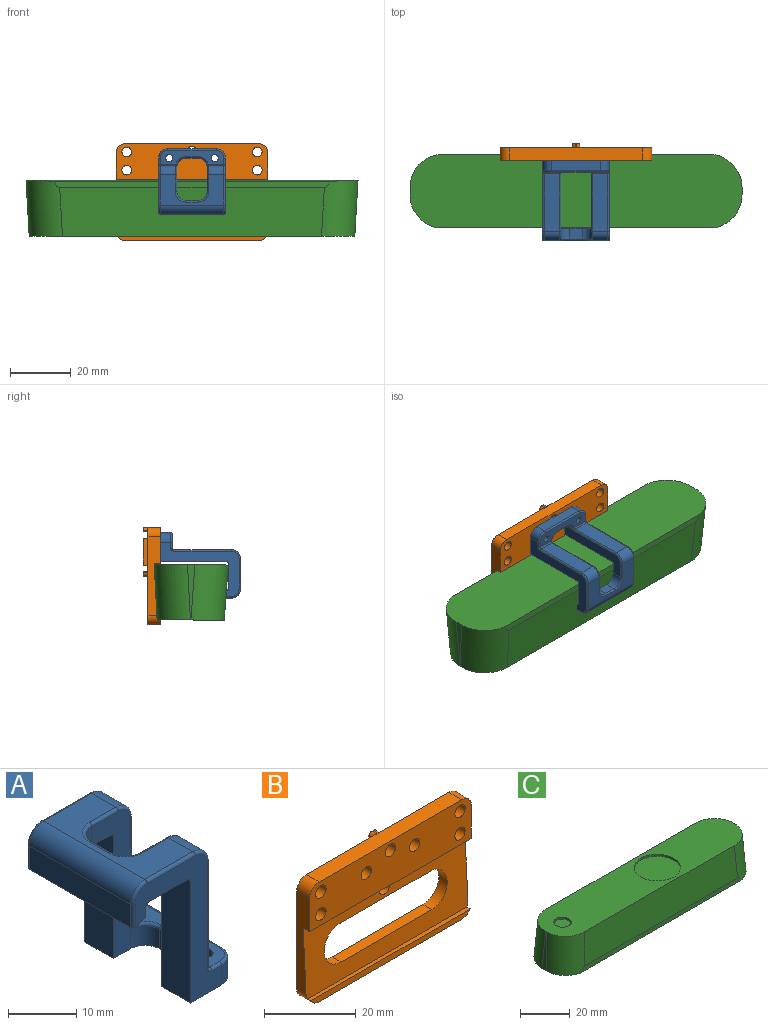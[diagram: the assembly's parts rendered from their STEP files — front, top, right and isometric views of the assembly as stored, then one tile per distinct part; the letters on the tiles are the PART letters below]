
ASSEMBLY  parts=3 mates=2
PART A: 65 faces, bbox 22x22.5x26.7 mm
  f0: cylinder r=3mm len=4.5mm, axis (0,0,1), area 16.7mm2, adj f3,f17,f20,f42,f45
  f1: plane 22x8.4mm, normal (0,0,-1), area 118.7mm2, adj f13,f14,f17,f18,f19,f24,f25,f62
  f2: plane 22x6mm, normal (-1,0,0), area 132mm2, adj f3,f13,f17,f64
  f3: plane 22x9.5mm, normal (0,0,-1), area 135mm2, adj f0,f2,f10,f11,f13,f14,f15,f16
  f4: plane 21x4.5mm, normal (0,0,1), area 60.4mm2, adj f15,f16,f38,f44,f45,f47,f48,f49
  f5: plane 19x5mm, normal (1,0,0), area 95mm2, adj f23,f37,f38,f39
  f6: plane 21x10mm, normal (0,0,1), area 116.3mm2, adj f22,f23,f26,f31,f32,f34,f36,f40
  f7: plane 21x4.19mm, normal (-1,0,0), area 88mm2, adj f8,f26,f29,f61
  f8: plane 22x2.6mm, normal (0.26,0,-0.97), area 59.1mm2, adj f7,f9,f13,f14,f29,f61
  f9: plane 22x2mm, normal (1,0,0), area 44mm2, adj f8,f13,f14,f63
  f10: plane 22x6mm, normal (-1,0,0), area 132mm2, adj f3,f14,f18,f62
  f11: plane 16x3.5mm, normal (1,0,0), area 56mm2, adj f3,f27,f28,f49
  f12: plane 19x5mm, normal (1,0,0), area 95mm2, adj f22,f51,f55,f57
  f13: plane 26x18mm, normal (0,-1,0), area 145.2mm2, adj f1,f2,f3,f8,f9,f28,f29,f30
  f14: plane 26x18mm, normal (0,1,0), area 145.2mm2, adj f1,f3,f8,f9,f10,f27,f54,f56
  f15: cylinder r=1.2mm len=4mm, axis (0,0,1), area 30.2mm2, adj f3,f4
  f16: cylinder r=1.2mm len=4mm, axis (0,0,1), area 30.2mm2, adj f3,f4
  f17: plane 26x8mm, normal (0,1,0), area 105.5mm2, adj f0,f1,f2,f3,f25,f31,f33,f39
  f18: plane 26x8mm, normal (0,-1,0), area 105.5mm2, adj f1,f3,f10,f21,f24,f43,f46,f51
  f19: plane 4x3.5mm, normal (1,0,0), area 14mm2, adj f1,f24,f25,f36
  f20: plane 4x3.5mm, normal (-1,0,0), area 14mm2, adj f0,f3,f21,f48
  f21: cylinder r=3mm len=4.5mm, axis (0,0,-1), area 16.7mm2, adj f3,f18,f20,f50,f53
  f22: cylinder r=3mm len=5mm, axis (0,1,0), area 23.6mm2, adj f6,f12,f46,f58
  f23: cylinder r=3mm len=5mm, axis (0,1,0), area 23.6mm2, adj f5,f6,f33,f35
  f24: cylinder r=3mm len=3.5mm, axis (0,0,1), area 16.5mm2, adj f1,f18,f19,f40
  f25: cylinder r=3mm len=3.5mm, axis (0,0,-1), area 16.5mm2, adj f1,f17,f19,f34
  f26: cylinder r=3mm len=21mm, axis (0,1,0), area 99mm2, adj f6,f7,f30,f60
  f27: cylinder r=3mm len=3.5mm, axis (0,0,1), area 16.5mm2, adj f3,f11,f14,f52
  f28: cylinder r=3mm len=3.5mm, axis (0,0,-1), area 16.5mm2, adj f3,f11,f13,f47
  f29: cylinder r=0.5mm len=4.19mm, axis (0,0,1), area 3.3mm2, adj f7,f8,f13,f30
  f30: torus R=2.5mm, axis (0,-1,0), area 3.5mm2, adj f13,f26,f29,f32
  f31: cylinder r=0.5mm len=5.5mm, axis (-1,0,0), area 4.3mm2, adj f6,f17,f33,f34
  f32: cylinder r=0.5mm len=10mm, axis (1,0,0), area 7.9mm2, adj f6,f13,f30,f35
  f33: torus R=2.5mm, axis (0,1,0), area 3.5mm2, adj f17,f23,f31,f39
  f34: torus R=3.5mm, axis (0,0,1), area 3.9mm2, adj f6,f25,f31,f36
  f35: torus R=2.5mm, axis (0,-1,0), area 3.5mm2, adj f13,f23,f32,f37
  f36: cylinder r=0.5mm len=4mm, axis (0,1,0), area 3.1mm2, adj f6,f19,f34,f40
  f37: cylinder r=0.5mm len=19mm, axis (0,0,-1), area 14.9mm2, adj f5,f13,f35,f41
  f38: cylinder r=0.5mm len=5.15mm, axis (0,-1,0), area 4mm2, adj f4,f5,f41,f42
  f39: cylinder r=0.5mm len=19mm, axis (0,0,1), area 14.9mm2, adj f5,f17,f33,f42
  f40: torus R=3.5mm, axis (0,0,1), area 3.9mm2, adj f6,f24,f36,f43
  f41: torus R=1mm, axis (0,-1,0), area 0.8mm2, adj f13,f37,f38,f44
  f42: bspline ~1.22x1.07mm, area 0.8mm2, adj f0,f38,f39,f45
  f43: cylinder r=0.5mm len=5.5mm, axis (1,0,0), area 4.3mm2, adj f6,f18,f40,f46
  f44: cylinder r=0.5mm len=2mm, axis (1,0,0), area 1.6mm2, adj f4,f13,f41,f47
  f45: torus R=3.5mm, axis (0,0,1), area 3.2mm2, adj f0,f4,f42,f48
  f46: torus R=2.5mm, axis (0,1,0), area 3.5mm2, adj f18,f22,f43,f51
  f47: torus R=2.5mm, axis (0,0,1), area 3.5mm2, adj f4,f28,f44,f49
  f48: cylinder r=0.5mm len=4mm, axis (0,-1,0), area 3.1mm2, adj f4,f20,f45,f50
  f49: cylinder r=0.5mm len=16mm, axis (0,1,0), area 12.6mm2, adj f4,f11,f47,f52
  f50: torus R=3.5mm, axis (0,0,1), area 3.2mm2, adj f4,f21,f48,f53
  f51: cylinder r=0.5mm len=19mm, axis (0,0,-1), area 14.9mm2, adj f12,f18,f46,f53
  f52: torus R=2.5mm, axis (0,0,1), area 3.5mm2, adj f4,f27,f49,f54
  f53: bspline ~1.14x1.11mm, area 0.8mm2, adj f21,f50,f51,f55
  f54: cylinder r=0.5mm len=2mm, axis (-1,0,0), area 1.6mm2, adj f4,f14,f52,f56
  f55: cylinder r=0.5mm len=5.15mm, axis (0,-1,0), area 4mm2, adj f4,f12,f53,f56
  f56: torus R=1mm, axis (0,-1,0), area 0.8mm2, adj f14,f54,f55,f57
  f57: cylinder r=0.5mm len=19mm, axis (0,0,1), area 14.9mm2, adj f12,f14,f56,f58
  f58: torus R=2.5mm, axis (0,-1,0), area 3.5mm2, adj f14,f22,f57,f59
  f59: cylinder r=0.5mm len=10mm, axis (-1,0,0), area 7.9mm2, adj f6,f14,f58,f60
  f60: torus R=2.5mm, axis (0,-1,0), area 3.5mm2, adj f14,f26,f59,f61
  f61: cylinder r=0.5mm len=4.19mm, axis (0,0,-1), area 3.3mm2, adj f7,f8,f14,f60
  f62: cylinder r=0.5mm len=6mm, axis (0,1,0), area 4.7mm2, adj f1,f10,f14,f18
  f63: cylinder r=0.5mm len=22mm, axis (0,-1,0), area 17.3mm2, adj f1,f9,f13,f14
  f64: cylinder r=0.5mm len=6mm, axis (0,1,0), area 4.7mm2, adj f1,f2,f13,f17
PART B: 39 faces, bbox 50x5.5x32 mm
  f0: plane 8.88x1.5mm, normal (1,0,0), area 13.3mm2, adj f4,f6,f33,f34
  f1: plane 1.5x0.44mm, normal (1,0,0), area 0.7mm2, adj f5,f6,f33,f35
  f2: plane 8.88x1.5mm, normal (-1,0,0), area 13.3mm2, adj f4,f6,f33,f34
  f3: plane 1.5x0.44mm, normal (-1,0,0), area 0.7mm2, adj f5,f6,f33,f36
  f4: plane 8.88x2.4mm, normal (0,1,0), area 19.5mm2, adj f0,f2,f33,f34
  f5: plane 2.4x1.44mm, normal (0,1,0), area 2.1mm2, adj f1,f3,f26,f33,f35,f36
  f6: plane 50x32mm, normal (0,1,0), area 1145.6mm2, adj f0,f1,f2,f3,f9,f10,f11,f12
  f7: plane 50x18.7mm, normal (0,-1,0.05), area 568.8mm2, adj f9,f10,f14,f15,f22,f23,f26,f27
  f8: plane 50x11.8mm, normal (0,-1,0), area 529.8mm2, adj f9,f10,f12,f15,f16,f17,f18,f19
  f9: plane 26x4mm, normal (1,0,0), area 77.7mm2, adj f6,f7,f8,f15,f23,f24
  f10: plane 26x4mm, normal (-1,0,0), area 77.7mm2, adj f6,f7,f8,f15,f22,f25
  f11: plane 44x4mm, normal (0,0,-1), area 176mm2, adj f6,f13,f22,f23
  f12: plane 44x5.5mm, normal (0,0,1), area 176.6mm2, adj f6,f8,f24,f25,f32,f37,f38
  f13: plane 49.2x1.5mm, normal (0,-1,0), area 71.5mm2, adj f11,f14,f22,f23
  f14: plane 49.2x1mm, normal (0,0,1), area 49.2mm2, adj f7,f13,f22,f23
  f15: plane 50x1.98mm, normal (0,0,-1), area 99mm2, adj f7,f8,f9,f10
  f16: cylinder r=1.6mm len=4mm, axis (0,-1,0), area 40.2mm2, adj f6,f8
  f17: cylinder r=1.6mm len=4mm, axis (0,-1,0), area 40.2mm2, adj f6,f8
  f18: cylinder r=1.6mm len=4mm, axis (0,-1,0), area 40.2mm2, adj f6,f8
  f19: cylinder r=1.6mm len=4mm, axis (0,-1,0), area 40.2mm2, adj f6,f8
  f20: cylinder r=1.6mm len=4mm, axis (0,-1,0), area 40.2mm2, adj f6,f8
  f21: cylinder r=1.6mm len=4mm, axis (0,-1,0), area 40.2mm2, adj f6,f8
  f22: cylinder r=3mm len=4mm, axis (0,-1,0), area 17.2mm2, adj f6,f7,f10,f11,f13,f14
  f23: cylinder r=3mm len=4mm, axis (0,1,0), area 17.2mm2, adj f6,f7,f9,f11,f13,f14
  f24: cylinder r=3mm len=4mm, axis (0,-1,0), area 18.8mm2, adj f6,f8,f9,f12
  f25: cylinder r=3mm len=4mm, axis (0,1,0), area 18.8mm2, adj f6,f8,f10,f12
  f26: plane 28x3.74mm, normal (0,0,-1), area 63.3mm2, adj f5,f6,f7,f28,f29,f35,f36
  f27: plane 28x2.76mm, normal (0,0,1), area 77.4mm2, adj f6,f7,f28,f29
  f28: cylinder r=5mm len=10mm, axis (0,1,0), area 39.3mm2, adj f6,f7,f26,f27
  f29: cylinder r=5mm len=10mm, axis (0,-1,0), area 39.3mm2, adj f6,f7,f26,f27
  f30: plane 1.5x0.44mm, normal (1,0,0), area 0.7mm2, adj f6,f32,f34,f38
  f31: plane 1.5x0.44mm, normal (-1,0,0), area 0.7mm2, adj f6,f32,f34,f37
  f32: plane 2.4x1.44mm, normal (0,1,0), area 2.1mm2, adj f12,f30,f31,f34,f37,f38
  f33: cylinder r=1.6mm len=3.69mm, axis (0,1,0), area 29.3mm2, adj f0,f1,f2,f3,f4,f5,f6,f7
  f34: cylinder r=1.6mm len=5.5mm, axis (0,1,0), area 48.4mm2, adj f0,f2,f4,f6,f8,f30,f31,f32
  f35: cylinder r=1mm len=1.5mm, axis (0,-1,0), area 2.4mm2, adj f1,f5,f6,f26
  f36: cylinder r=1mm len=1.5mm, axis (0,1,0), area 2.4mm2, adj f3,f5,f6,f26
  f37: cylinder r=1mm len=1.5mm, axis (0,1,0), area 2.4mm2, adj f6,f12,f31,f32
  f38: cylinder r=1mm len=1.5mm, axis (0,-1,0), area 2.4mm2, adj f6,f12,f30,f32
PART C: 16 faces, bbox 109.4x24.4x18.8 mm
  f0: plane 18.23x2.44mm, normal (-1,0,0.06), area 23.8mm2, adj f1,f3,f8,f9
  f1: plane 109.4x24.13mm, normal (0,0,-1), area 2541.9mm2, adj f0,f2,f4,f5,f8,f9,f10,f11
  f2: plane 18.23x2.44mm, normal (1,0,0.06), area 23.8mm2, adj f1,f3,f10,f11
  f3: plane 107.31x22.13mm, normal (0,0,1), area 1960.5mm2, adj f0,f2,f6,f7,f8,f9,f10,f11
  f4: plane 90.94x2.23mm, normal (0,-1,0), area 199.9mm2, adj f1,f7,f9,f11
  f5: plane 90.94x2.23mm, normal (0,1,0), area 199.9mm2, adj f1,f6,f8,f10
  f6: plane 87.19x16mm, normal (0,1,0.06), area 1383mm2, adj f3,f5,f8,f10
  f7: plane 87.19x16mm, normal (0,-1,0.06), area 1383mm2, adj f3,f4,f9,f11
  f8: cylinder r=11mm len=18.83mm, axis (-0.06,0.06,-1), area 312.8mm2, adj f0,f1,f3,f5,f6
  f9: cylinder r=11mm len=18.83mm, axis (-0.06,-0.06,-1), area 312.8mm2, adj f0,f1,f3,f4,f7
  f10: cylinder r=11mm len=18.83mm, axis (-0.06,-0.06,1), area 312.8mm2, adj f1,f2,f3,f5,f6
  f11: cylinder r=11mm len=18.83mm, axis (-0.06,0.06,1), area 312.8mm2, adj f1,f2,f3,f4,f7
  f12: cylinder r=9.31mm len=18.63mm, axis (0,0,1), area 58.5mm2, adj f3,f13
  f13: plane 18.63x18.63mm, normal (0,0,1), area 272.5mm2, adj f12
  f14: cylinder r=3.5mm len=7mm, axis (0,0,1), area 22mm2, adj f3,f15
  f15: plane 7x7mm, normal (0,0,1), area 38.5mm2, adj f14
PLACE A rot(axis=(0.58,-0.58,0.58),120deg) t=(0,-4,4.7)mm
PLACE B at identity fixed
PLACE C rot(axis=(-1,0,0),179.4deg) t=(0,-14.24,3.74)mm
MATE fastened A.f15 <-> B.f17  axis (0,1,0) through (7.5,-4,11.2)mm
MATE fastened C.f7 <-> B.f7  axis (0,1,-0.05) through (0,-2.57,-6.35)mm
